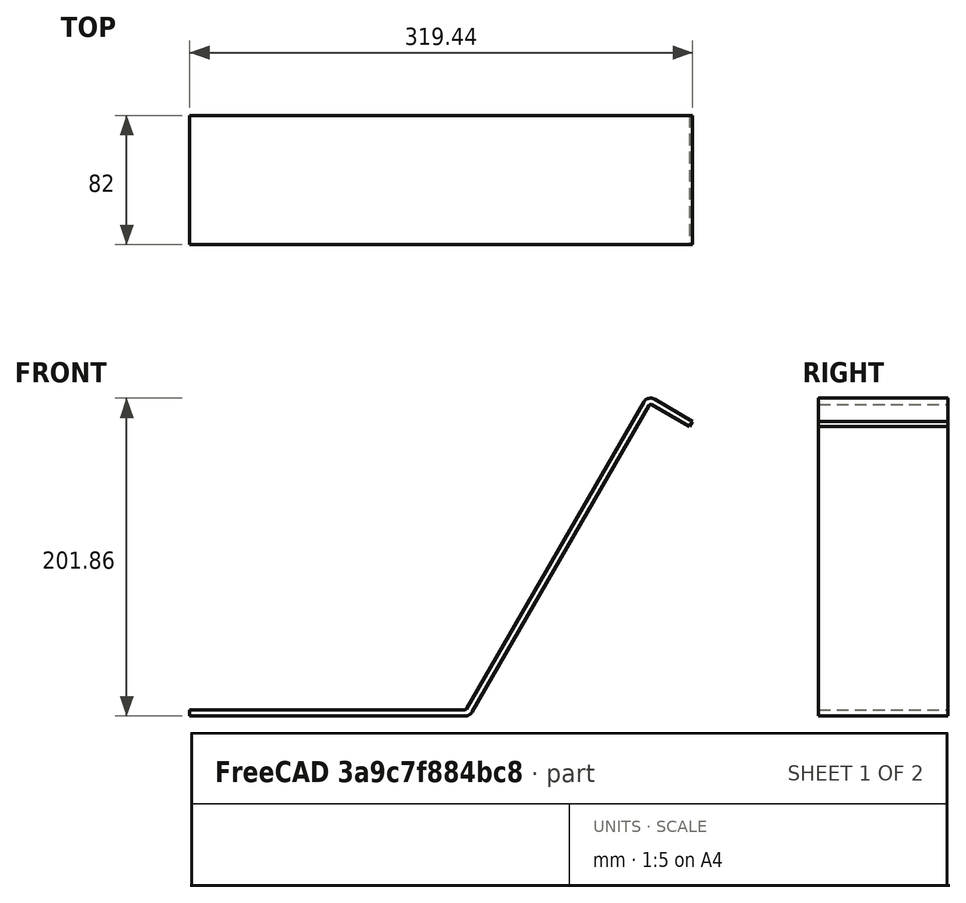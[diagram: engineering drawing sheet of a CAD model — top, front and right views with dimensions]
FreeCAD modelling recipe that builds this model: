
FCSTD DOCUMENT  (FreeCAD 0.20R29603 (Git))
Label: SupportAcierPedaleExpression
License: All rights reserved
LicenseURL: http://en.wikipedia.org/wiki/All_rights_reserved
objects: TechDraw::DrawViewDimension×7, PartDesign::FeaturePython×3, TechDraw::DrawViewPart×2, App::Part×1, Sketcher::SketchObject×1, PartDesign::Pad×1, PartDesign::Body×1, TechDraw::DrawSVGTemplate×1, TechDraw::DrawPage×1
note: 7 computed .brp shape members not serialized (recipe doc carries the construction recipe); baked Part::Feature solids carry a one-line shape summary decoded from their .brp

FEATURE [App::Part] Part
  Origin = -> Origin
FEATURE [Sketcher::SketchObject] Sketch
  FullyConstrained = true
  MapMode = 5
  Support = -> [XY_Plane001]
  sketch-geometry (4):
    g0: LineSegment StartX=0 StartY=82 StartZ=0 EndX=175 EndY=82 EndZ=0
    g1: LineSegment StartX=175 StartY=82 StartZ=0 EndX=175 EndY=0 EndZ=0
    g2: LineSegment StartX=175 StartY=0 StartZ=0 EndX=0 EndY=0 EndZ=0
    g3: LineSegment StartX=0 StartY=0 StartZ=0 EndX=0 EndY=82 EndZ=0
  constraints (11):
    c: Coincident(g0,g1)
    c: Coincident(g1,g2)
    c: Coincident(g2,g3)
    c: Coincident(g3,g0)
    c: Horizontal(g0)
    c: Horizontal(g2)
    c: Vertical(g1)
    c: Vertical(g3)
    c: Coincident(g2,g-1)
    c: DistanceX(g0,g0) = 175
    c: DistanceY(g1,g1) = 82
FEATURE [PartDesign::Pad] Pad
  Direction = (0,0,1)
  Length = 4
  Length2 = 10
  Profile = -> Sketch
  ReferenceAxis = -> Sketch [N_Axis]
  Type = 0
FEATURE [PartDesign::FeaturePython] Bend  # WARN: FeaturePython — macro-defined, semantics opaque (R4)
  AutoMiter = true
  BaseFeature = -> Pad
  BendType = 0
  LengthList = [10]
  LengthSpec = 0
  ReliefFactor = 0.7
  UseReliefFactor = false
  angle = 60
  baseObject = -> Pad [Face2]
  bendAList = [60]
  extend1 = 0
  extend2 = 0
  gap1 = 0
  gap2 = 0
  invert = false
  kfactor = 0.5
  length = 10
  maxExtendDist = 5
  minGap = 0.1
  minReliefGap = 1
  miterangle1 = 0
  miterangle2 = 0
  offset = 0
  radius = 1
  reliefType = 0
  reliefd = 1
  reliefw = 0.8
  sketchflip = false
  sketchinvert = false
  unfold = false
FEATURE [PartDesign::FeaturePython] Extend  # WARN: FeaturePython — macro-defined, semantics opaque (R4)
  BaseFeature = -> Bend
  Offset = 0.02
  Refine = true
  UseSubtraction = false
  baseObject = -> Bend [Face3]
  gap1 = 0
  gap2 = 0
  length = 215
FEATURE [PartDesign::FeaturePython] Bend001  # WARN: FeaturePython — macro-defined, semantics opaque (R4)
  AutoMiter = true
  BaseFeature = -> Extend
  BendType = 0
  LengthList = [28]
  LengthSpec = 0
  ReliefFactor = 0.7
  UseReliefFactor = false
  angle = 90
  baseObject = -> Extend [Face7]
  bendAList = [90]
  extend1 = 0
  extend2 = 0
  gap1 = 0
  gap2 = 0
  invert = true
  kfactor = 0.5
  length = 28
  maxExtendDist = 5
  minGap = 0.1
  minReliefGap = 1
  miterangle1 = 0
  miterangle2 = 0
  offset = 0
  radius = 1
  reliefType = 0
  reliefd = 1
  reliefw = 0.8
  sketchflip = false
  sketchinvert = false
  unfold = false
FEATURE [PartDesign::Body] Body
  Group = -> [Sketch,Pad,Bend,Extend,Bend001]
  Origin = -> Origin001
  Tip = -> Bend001
FEATURE [TechDraw::DrawSVGTemplate] Template
  Height = 210
  Orientation = 1
  Width = 297
FEATURE [TechDraw::DrawViewPart] View  label="Vue de profil"
  CoarseView = false
  Direction = (0,-1,0)
  Focus = 100
  HardHidden = false
  IsoCount = 0
  IsoHidden = false
  IsoVisible = false
  LockPosition = false
  Perspective = false
  Rotation = 0
  Scale = 0.5
  ScaleType = 0
  SeamHidden = false
  SeamVisible = false
  SmoothHidden = false
  SmoothVisible = false
  Source = -> [Body]
  X = 141.667
  XDirection = (1,0,0)
  Y = 68.7852
FEATURE [TechDraw::DrawViewDimension] Dimension
  AngleOverride = false
  Arbitrary = false
  ArbitraryTolerances = false
  EqualTolerance = true
  ExtensionAngle = 0
  FormatSpec = %.2w
  FormatSpecOverTolerance = %+.2w
  FormatSpecUnderTolerance = %+.2w
  Inverted = false
  LineAngle = 0
  LockPosition = false
  MeasureType = 1
  OverTolerance = 0
  References2D = -> [View]
  Rotation = 0
  Scale = 0.5
  ScaleType = 0
  TheoreticalExact = false
  Type = 6
  UnderTolerance = 0
  X = -9.25359
  Y = -16.076
FEATURE [TechDraw::DrawViewDimension] Dimension001
  AngleOverride = false
  Arbitrary = false
  ArbitraryTolerances = false
  EqualTolerance = true
  ExtensionAngle = 0
  FormatSpec = %.2w
  FormatSpecOverTolerance = %+.2w
  FormatSpecUnderTolerance = %+.2w
  Inverted = false
  LineAngle = 0
  LockPosition = false
  MeasureType = 1
  OverTolerance = 0
  References2D = -> [View]
  Rotation = 0
  Scale = 0.5
  ScaleType = 0
  TheoreticalExact = false
  Type = 1
  UnderTolerance = 0
  X = -34.2399
  Y = -29.1199
FEATURE [TechDraw::DrawViewDimension] Dimension002
  AngleOverride = false
  Arbitrary = false
  ArbitraryTolerances = false
  EqualTolerance = true
  ExtensionAngle = 0
  FormatSpec = %.2w
  FormatSpecOverTolerance = %+.2w
  FormatSpecUnderTolerance = %+.2w
  Inverted = false
  LineAngle = 0
  LockPosition = false
  MeasureType = 1
  OverTolerance = 0
  References2D = -> [View]
  Rotation = 0
  Scale = 0.5
  ScaleType = 0
  TheoreticalExact = false
  Type = 0
  UnderTolerance = 0
  X = 55.3942
  Y = -7.04207
FEATURE [TechDraw::DrawViewDimension] Dimension003
  AngleOverride = false
  Arbitrary = false
  ArbitraryTolerances = false
  EqualTolerance = true
  ExtensionAngle = 0
  FormatSpec = %.2w
  FormatSpecOverTolerance = %+.2w
  FormatSpecUnderTolerance = %+.2w
  Inverted = false
  LineAngle = 0
  LockPosition = false
  MeasureType = 1
  OverTolerance = 0
  References2D = -> [View]
  Rotation = 0
  Scale = 0.5
  ScaleType = 0
  TheoreticalExact = false
  Type = 0
  UnderTolerance = 0
  X = 85.4331
  Y = 18.3411
FEATURE [TechDraw::DrawViewDimension] Dimension004
  AngleOverride = false
  Arbitrary = false
  ArbitraryTolerances = false
  EqualTolerance = true
  ExtensionAngle = 0
  FormatSpec = %.2w
  FormatSpecOverTolerance = %+.2w
  FormatSpecUnderTolerance = %+.2w
  Inverted = false
  LineAngle = 0
  LockPosition = false
  MeasureType = 1
  OverTolerance = 0
  References2D = -> [View]
  Rotation = 0
  Scale = 0.5
  ScaleType = 0
  TheoreticalExact = false
  Type = 2
  UnderTolerance = 0
  X = -87.486
  Y = -37.9789
FEATURE [TechDraw::DrawViewPart] View001  label="Vue de dessus"
  CoarseView = false
  Direction = (0,0,1)
  Focus = 100
  HardHidden = false
  IsoCount = 0
  IsoHidden = false
  IsoVisible = false
  LockPosition = false
  Perspective = false
  Rotation = 0
  Scale = 0.5
  ScaleType = 0
  SeamHidden = false
  SeamVisible = false
  SmoothHidden = false
  SmoothVisible = false
  Source = -> [Body]
  X = 141.557
  XDirection = (1,0,0)
  Y = 165.357
FEATURE [TechDraw::DrawViewDimension] Dimension005
  AngleOverride = false
  Arbitrary = false
  ArbitraryTolerances = false
  EqualTolerance = true
  ExtensionAngle = 0
  FormatSpec = %.2w
  FormatSpecOverTolerance = %+.2w
  FormatSpecUnderTolerance = %+.2w
  Inverted = false
  LineAngle = 0
  LockPosition = false
  MeasureType = 1
  OverTolerance = 0
  References2D = -> [View]
  Rotation = 0
  Scale = 0.5
  ScaleType = 0
  TheoreticalExact = false
  Type = 6
  UnderTolerance = 0
  X = 77.1557
  Y = 6.26356
FEATURE [TechDraw::DrawViewDimension] Dimension006
  AngleOverride = false
  Arbitrary = false
  ArbitraryTolerances = false
  EqualTolerance = true
  ExtensionAngle = 0
  FormatSpec = %.2w
  FormatSpecOverTolerance = %+.2w
  FormatSpecUnderTolerance = %+.2w
  Inverted = false
  LineAngle = 0
  LockPosition = false
  MeasureType = 1
  OverTolerance = 0
  References2D = -> [View001]
  Rotation = 0
  Scale = 0.5
  ScaleType = 0
  TheoreticalExact = false
  Type = 2
  UnderTolerance = 0
  X = -96.3742
  Y = 2.21529
FEATURE [TechDraw::DrawPage] Page
  KeepUpdated = true
  NextBalloonIndex = 1
  ProjectionType = 0
  Scale = 0.5
  Template = -> Template
  Views = -> [View,Dimension,Dimension001,Dimension002,Dimension003,Dimension004,View001,Dimension005,Dimension006]
